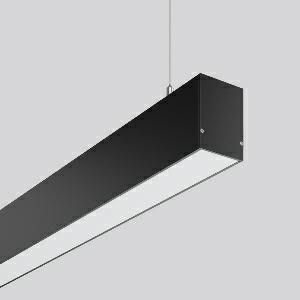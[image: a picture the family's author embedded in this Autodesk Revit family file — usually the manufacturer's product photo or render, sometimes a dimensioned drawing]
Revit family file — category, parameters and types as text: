
# Revit family: less_is_more_50_312321_003_1_76_8328
name_source: partatom
category: Lighting Fixtures
units: mm (PartAtom-declared; Revit-internal decimal feet)

## family parameters
Cut with Voids When Loaded = No
Host = Face
Light Source = No
Part Type = Normal
Room Calculation Point = No
Round Connector Dimension = Use Diameter
Shared = No

## types (1)
- LESS IS MORE 50 (1 x LED Modul 840, 8850 lm, 4000)
    Apparent Load = 74 VA
    CIE Flux Codes = 49 80 96 63 100
    Color Rendering = 80
    Color Temperature = 4000
    Default Elevation = 1800 mm
    Description = Series: LESS IS MORE 50
Linear pendant luminaire for aesthetically sophisticated lighting. Housing: extruded aluminium profile, powder-coated. End cap aluminium powder-coated. Canopy made of aluminium, powder-coated. Diffuser made of non-yellowing plastic (PMMA), opal. Direct 65%, indirect 35% light emission. Controlled separately. Suitable for pendant. 2-point steel cable suspension freely positionable and infinitely height-adjustable. Special lengths available on request. LED unit with integrated converter interchangeable and removable. Suitable for through-wiring. With sensors or as a safety luminaire on request. 
Colour: deep black, matt (RAL 9005)
Length: 1967 mm
Width: 57 mm
Height: 75 mm
Suspension length: 2000 mm
Lamp: LED
Socket: without socket
Colour temperature: 4000K
Colour rendering index (CRI): 80
Light source: LED
Socket lamp2: Without base
Colour temperature: 4000K
System power: 74 W
Rated luminous flux: 8850 lm
Luminous efficiency: 120 lm/W
Control gear: Converter, dimmable, DALI
Control gear: Converter, dimmable, DALI
Protection class: I
Type of protection: IP 20
    Height = 75 mm
    Lamp = 1 x LED Modul 840
    Lamp Light Flux = 8850 lm
    Lamp count = 1
    Length = 1967 mm
    Lifetime = 50000 h
    Luminous efficacy = 120 lm/W
    Manufacturer = RZB
    ModVariant = No
    Model = 312321.003.1.76
    Mounting Place = Ceiling
    Mounting Type = Pendant
    Number of Poles = 1
    OnlyDefault = Yes
    Power Factor = 1
    Product Name = LESS IS MORE 50
    Product group = Pendant LED linear luminaires
    ProductGroupID = 907
    Protection Class = Protection class I
    Protection Degree = IP 20
    RLX_Detail_Level = 1
    RLX_Emergency_Light_Flux = 0 lm
    RLX_Emergency_Type = 0
    RLX_Emergency_Type_DB = No
    RlxData = <blob elided: 39965 chars, md5=767aefcb>
    Socket = socket
    Standby Power = 0 W
    System Light Flux = 8850 lm
    System Power = 74 W
    Type Comments = Product without accessories
    Type Image = 312318.003.jpg
    URL = http://relux.com
    VarID = ---
    Voltage = 230 V
    Voltage Range = 220-240 V
    Weight = 0.00 kg
    Width = 57 mm

## geometry (parser evidence)
native form markers: Blend x4, Sweep x15
no freeform markers — native parametric forms only
